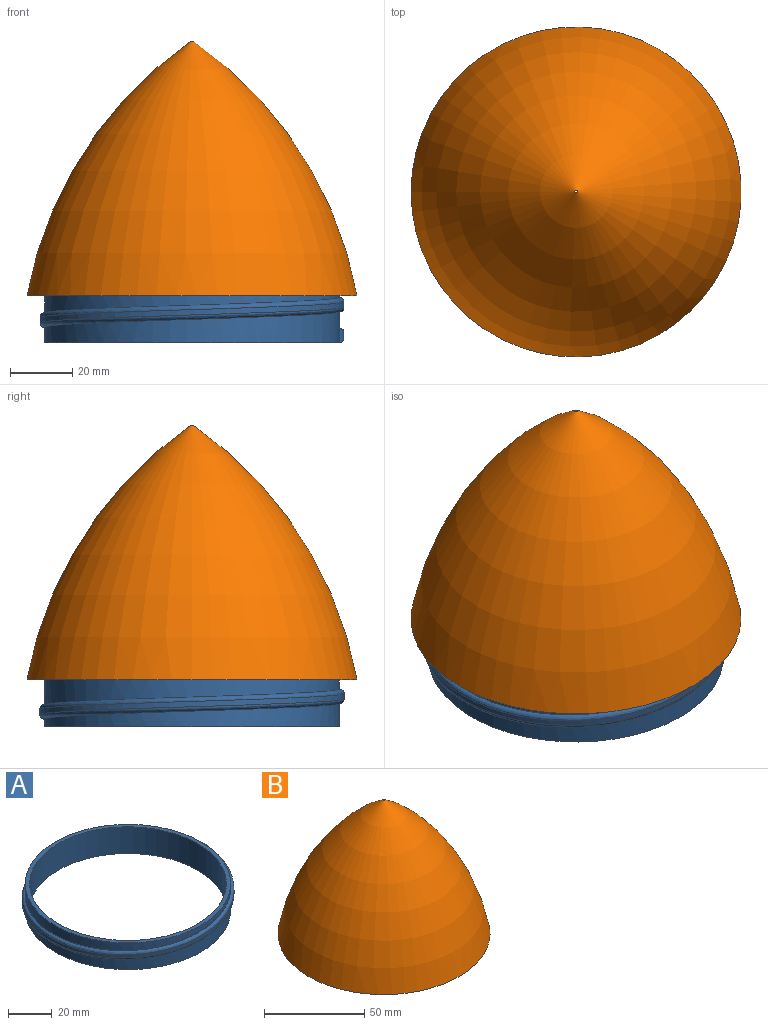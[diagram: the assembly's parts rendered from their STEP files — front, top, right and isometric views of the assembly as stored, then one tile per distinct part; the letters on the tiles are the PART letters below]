
ASSEMBLY  parts=2 mates=1
PART A: 12 faces, bbox 97.5x97.5x15 mm
  f0: cylinder r=47.25mm len=94.5mm, axis (0,0,-1), area 1632.8mm2, adj f1,f3,f5,f11
  f1: cylinder r=47.25mm len=94.5mm, axis (0,0,-1), area 1484.4mm2, adj f0,f4,f9,f10
  f2: cylinder r=45.25mm len=90.5mm, axis (0,0,-1), area 4264.7mm2, adj f3,f4
  f3: plane 94.5x94.5mm, normal (0,0,1), area 581.2mm2, adj f0,f2
  f4: plane 94.5x94.5mm, normal (0,0,-1), area 581.2mm2, adj f1,f2
  f5: bspline ~94.7x94.7mm, area 29.7mm2, adj f0,f6,f10,f11
  f6: bspline ~97.5x97.5mm, area 658.9mm2, adj f5,f7,f10,f11
  f7: cylinder r=48.75mm len=97.5mm, axis (0,0,1), area 507.7mm2, adj f6,f8,f10,f11
  f8: bspline ~97.5x97.5mm, area 659.2mm2, adj f7,f9,f10,f11
  f9: bspline ~94.7x94.7mm, area 29.7mm2, adj f1,f8,f10,f11
  f10: cylinder r=5mm len=4.51mm, axis (0,0,1), area 14.4mm2, adj f1,f5,f6,f7,f8,f9
  f11: cylinder r=5mm len=4.51mm, axis (0,0,1), area 14.4mm2, adj f0,f5,f6,f7,f8,f9
PART B: 6 faces, bbox 105.7x105.7x81.5 mm
  f0: revolved ~102.12x102.12mm, area 18456.9mm2, adj f2,f5
  f1: revolved ~105.74x105.74mm, area 20032.2mm2, adj f4,f5
  f2: plane 102.12x102.12mm, normal (0,0,1), area 1758.5mm2, adj f0,f3
  f3: cylinder r=45.25mm len=90.5mm, axis (0,0,-1), area 426.5mm2, adj f2,f4
  f4: plane 105.74x105.74mm, normal (0,0,-1), area 2348.7mm2, adj f1,f3
  f5: cylinder r=0.4mm len=1.83mm, axis (0,0,-1), area 4.6mm2, adj f0,f1
PLACE A at identity
PLACE B at identity
MATE fastened B.f3 <-> A.f2  axis (0,0,-1) through (0,0,15)mm
